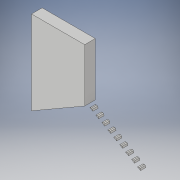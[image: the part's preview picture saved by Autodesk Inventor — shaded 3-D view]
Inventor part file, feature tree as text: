
AUTODESK INVENTOR PART (.ipt)
format: ipt  version: 2017 (Build 210142000, 142)  size: 293,888 bytes
history: native  units: in
note: dims shown in document units (in); Inventor stores cm internally (conversion verified against a paired STEP export)
features: extrude x3, sketch x1
ambient origin geometry x8: Origin, YZ Plane, XZ Plane, XY Plane, X Axis, Y Axis, Z Axis, Center Point
bodies: Solid1 (feature_tree)
feature tree (4):
  extrude  "door"  Depth=1.0in
  sketch  "Sketch3"  dims[d143=10.0in d144=0.0in d282=1.0in d283=1.0in d284=1.5in d285=1.5in d350=1.5in d351=1.0in d352=1.5in d353=0.9496in d356=0.9496in d358=1.0in d359=1.0in d360=1.0in d361=1.5in d362=1.5in d363=1.5in d364=1.0in d365=1.5in d366=0.9496in d367=0.9496in d368=1.0in d369=1.0in d370=1.0in d371=1.5in d372=1.5in d373=1.5in d374=1.0in d375=1.5in d376=0.9496in d377=0.9496in d378=1.0in d379=1.0in d380=1.0in d381=1.5in d382=1.5in d383=1.5in d384=1.0in d385=1.5in d386=0.9496in d387=0.9496in d388=1.0in d389=1.0in d390=1.0in d391=1.5in d392=1.5in d393=1.5in d394=1.0in d395=1.5in d396=0.9496in d397=0.9496in d398=1.0in d399=1.0in d400=1.0in d401=1.5in d402=1.5in d403=1.5in d404=1.0in d405=1.5in d406=0.9496in d407=0.9496in d408=1.0in d409=1.0in d410=1.0in d411=1.5in d412=1.5in d413=1.5in d414=1.0in d415=1.5in d416=0.9496in d417=0.9496in d418=1.0in d419=1.0in d420=1.0in d421=1.5in d422=1.5in d423=1.5in d424=1.0in d425=1.5in d426=0.9496in d427=0.9496in d428=1.0in d429=1.0in d430=1.0in d431=1.5in d432=1.5in d436=0.9496in d439=5.0in d440=0.0in d441=5.0in d442=0.0in d446=78.8675in]
  extrude  "connection give"  Depth=5.0in
  extrude  "connection receive"  Depth=1.0in
